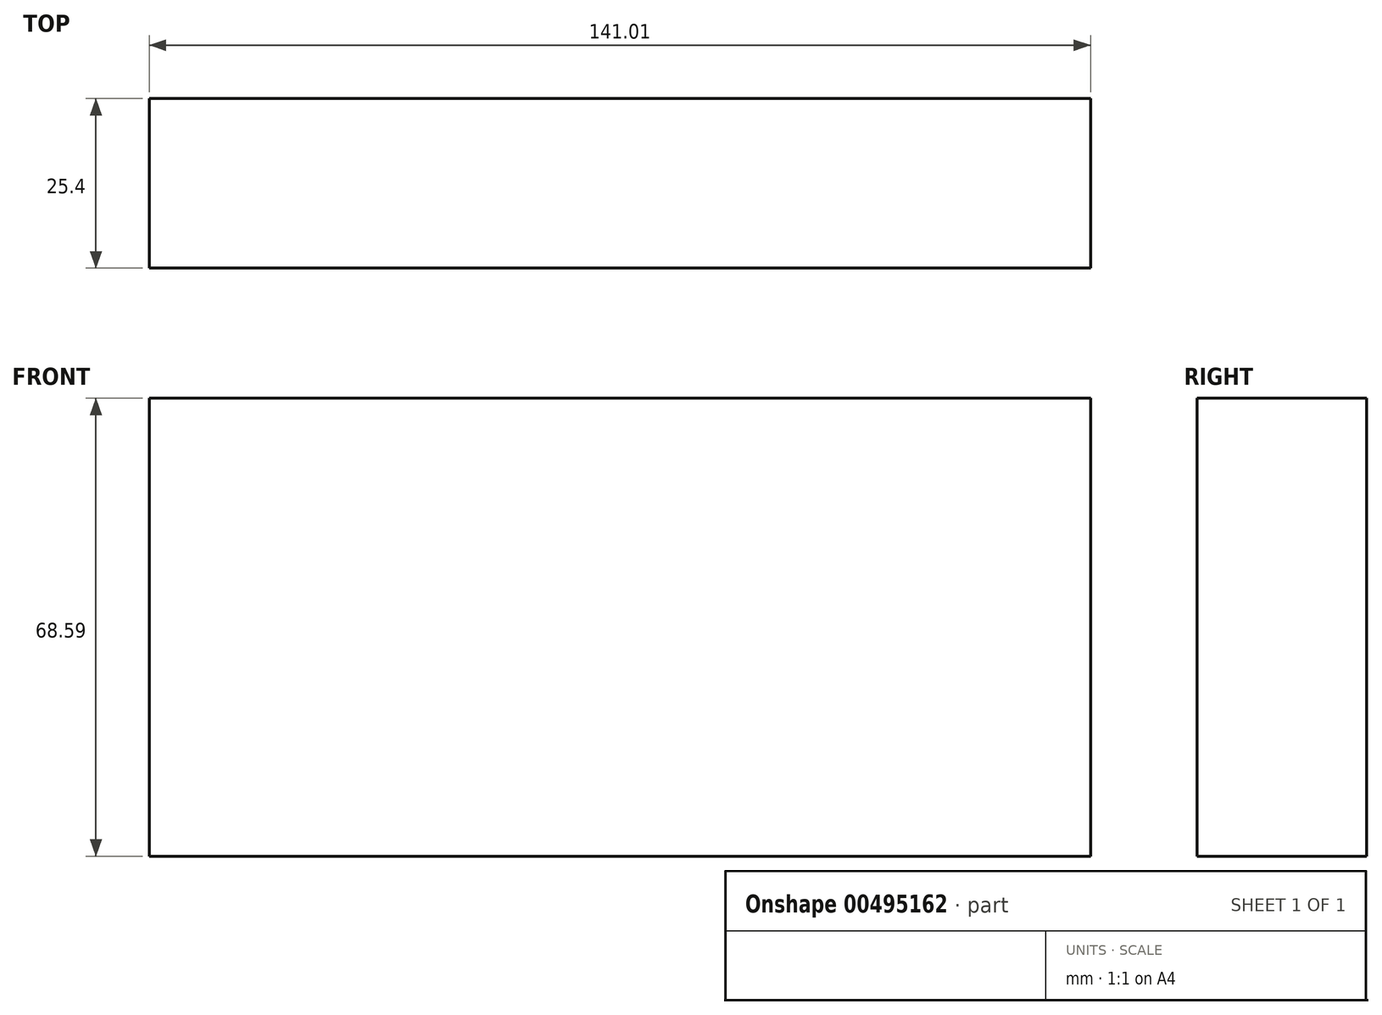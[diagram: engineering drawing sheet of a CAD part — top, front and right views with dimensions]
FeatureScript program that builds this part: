
annotation { "Feature Type Name" : "Feature", "Feature Type Description" : "" }
export const myFeature = defineFeature(function(context is Context, id is Id, definition is map)
    precondition{}
    {
        {
            var Q0;
            Q0=qCreatedBy(makeId("Front.planeOp"),FACE);
            var sketch = newSketch(context, id + "F0", { "sketchPlane" : qUnion([Q0])});
            skLineSegment(sketch, "E0.bottom", {"start": v(-66.36, 48.65) * mm, "end": v(74.65, 48.65) * mm});
            skLineSegment(sketch, "E0.top", {"start": v(-66.36, -19.94) * mm, "end": v(74.65, -19.94) * mm});
            skLineSegment(sketch, "E0.left", {"start": v(-66.36, 48.65) * mm, "end": v(-66.36, -19.94) * mm});
            skLineSegment(sketch, "E0.right", {"start": v(74.65, 48.65) * mm, "end": v(74.65, -19.94) * mm});
            skSolve(sketch);
        }
        {
            var Q0;
            Q0=makeQuery(id+"F0.imprint","IMPRINT",FACE,{"disambiguationData":[TD([[makeQuery(id+"F0.imprint","IMPRINT",EDGE,{"derivedFrom":sQuery(id+"F0.wireOp",EDGE,"E0.bottom")}),-1.0]])]});
            extrude(context, id + "F1", {"entities" : qUnion([Q0]), "depth" : 25.4 * mm});
        }
    });
